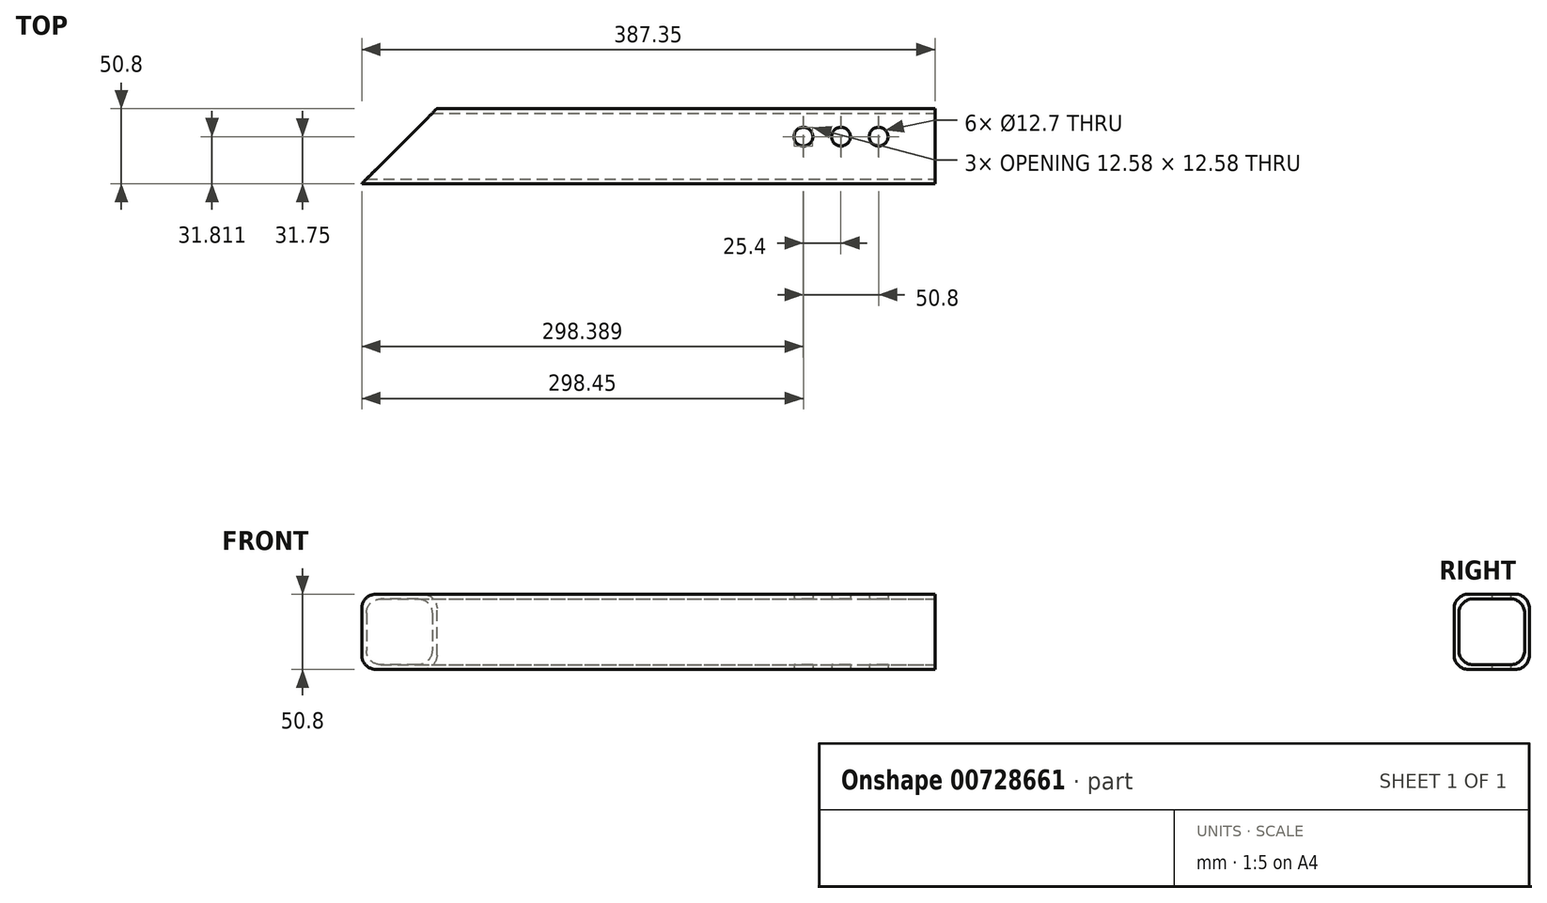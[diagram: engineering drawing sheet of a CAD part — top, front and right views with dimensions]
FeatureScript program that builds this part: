
annotation { "Feature Type Name" : "Feature", "Feature Type Description" : "" }
export const myFeature = defineFeature(function(context is Context, id is Id, definition is map)
    precondition{}
    {
        {
            var Q0;
            Q0=qCreatedBy(makeId("Right.planeOp"),FACE);
            var sketch = newSketch(context, id + "F0", { "sketchPlane" : qUnion([Q0])});
            skLineSegment(sketch, "E0.bottom", {"start": v(0, 0) * mm, "end": v(50.8, 0) * mm});
            skLineSegment(sketch, "E0.top", {"start": v(0, 50.8) * mm, "end": v(50.8, 50.8) * mm});
            skLineSegment(sketch, "E0.left", {"start": v(0, 0) * mm, "end": v(0, 50.8) * mm});
            skLineSegment(sketch, "E0.right", {"start": v(50.8, 0) * mm, "end": v(50.8, 50.8) * mm});
            skSolve(sketch);
        }
        {
            var Q0;
            Q0=qSketchRegion(id+"F0",true);
            extrude(context, id + "F1", {"entities" : qUnion([Q0]), "oppositeDirection" : true, "depth" : 387.35 * mm, "offsetDistance" : 25.4 * mm});
        }
        {
            var Q0;
            Q0=makeQuery(id+"F1.opExtrude","CAP_EDGE",EDGE,{"disambiguationData":[OSD([sQuery(id+"F0.wireOp",EDGE,"E0.right")])],"isStart":false});
            chamfer(context, id + "F2", {"entities" : qUnion([Q0]), "width" : 50.8 * mm, "tangentPropagation" : true});
        }
        {
            var Q0;
            Q0=makeQuery(id+"F1.opExtrude","CAP_FACE",FACE,{"disambiguationData":[OSD([sQuery(id+"F0.wireOp",EDGE,"E0.bottom"),sQuery(id+"F0.wireOp",EDGE,"E0.top"),sQuery(id+"F0.wireOp",EDGE,"E0.left"),sQuery(id+"F0.wireOp",EDGE,"E0.right")])],"isStart":true});
            var sketch = newSketch(context, id + "F3", { "sketchPlane" : qUnion([Q0])});
            skLineSegment(sketch, "E1.0", {"start": v(3.17, 47.63) * mm, "end": v(47.63, 47.63) * mm});
            skLineSegment(sketch, "E1.1", {"start": v(3.17, 3.17) * mm, "end": v(3.17, 47.63) * mm});
            skLineSegment(sketch, "E1.2", {"start": v(3.17, 3.17) * mm, "end": v(47.63, 3.17) * mm});
            skLineSegment(sketch, "E1.3", {"start": v(47.63, 3.17) * mm, "end": v(47.63, 47.63) * mm});
            skSolve(sketch);
        }
        {
            var Q0;
            Q0=qSketchRegion(id+"F3",true);
            extrude(context, id + "F4", {"entities" : qUnion([Q0]), "operationType" : NewBodyOperationType.REMOVE, "oppositeDirection" : true, "depth" : 876.3 * mm, "offsetDistance" : 25.4 * mm});
        }
        {
            var Q0;
            Q0=makeQuery(id+"F4.boolean.opBoolean","COPY",EDGE,{"derivedFrom":makeQuery(id+"F4.opExtrude","SWEPT_EDGE",EDGE,{"disambiguationData":[OSD([sQuery(id+"F3.wireOp",EDGE,"E1.1"),sQuery(id+"F3.wireOp",EDGE,"E1.2")])]})});
            var Q1;
            Q1=makeQuery(id+"F4.boolean.opBoolean","COPY",EDGE,{"derivedFrom":makeQuery(id+"F4.opExtrude","SWEPT_EDGE",EDGE,{"disambiguationData":[OSD([sQuery(id+"F3.wireOp",EDGE,"E1.2"),sQuery(id+"F3.wireOp",EDGE,"E1.3")])]})});
            var Q2;
            Q2=makeQuery(id+"F4.boolean.opBoolean","COPY",EDGE,{"derivedFrom":makeQuery(id+"F4.opExtrude","SWEPT_EDGE",EDGE,{"disambiguationData":[OSD([sQuery(id+"F3.wireOp",EDGE,"E1.0"),sQuery(id+"F3.wireOp",EDGE,"E1.3")])]})});
            var Q3;
            Q3=makeQuery(id+"F4.boolean.opBoolean","COPY",EDGE,{"derivedFrom":makeQuery(id+"F4.opExtrude","SWEPT_EDGE",EDGE,{"disambiguationData":[OSD([sQuery(id+"F3.wireOp",EDGE,"E1.0"),sQuery(id+"F3.wireOp",EDGE,"E1.1")])]})});
            var Q4;
            Q4=makeQuery(id+"F1.opExtrude","SWEPT_EDGE",EDGE,{"disambiguationData":[OSD([sQuery(id+"F0.wireOp",EDGE,"E0.bottom"),sQuery(id+"F0.wireOp",EDGE,"E0.right")])]});
            var Q5;
            Q5=makeQuery(id+"F1.opExtrude","SWEPT_EDGE",EDGE,{"disambiguationData":[OSD([sQuery(id+"F0.wireOp",EDGE,"E0.top"),sQuery(id+"F0.wireOp",EDGE,"E0.right")])]});
            var Q6;
            Q6=makeQuery(id+"F1.opExtrude","SWEPT_EDGE",EDGE,{"disambiguationData":[OSD([sQuery(id+"F0.wireOp",EDGE,"E0.top"),sQuery(id+"F0.wireOp",EDGE,"E0.left")])]});
            var Q7;
            Q7=makeQuery(id+"F1.opExtrude","SWEPT_EDGE",EDGE,{"disambiguationData":[OSD([sQuery(id+"F0.wireOp",EDGE,"E0.bottom"),sQuery(id+"F0.wireOp",EDGE,"E0.left")])]});
            fillet(context, id + "F5", {"entities" : qUnion([Q0, Q1, Q2, Q3, Q4, Q5, Q6, Q7]), "radius" : 9.52 * mm, "tangentPropagation" : true, "allowEdgeOverflow" : false});
        }
        {
            var Q0;
            Q0=makeQuery(id+"F1.opExtrude","SWEPT_FACE",FACE,{"disambiguationData":[OSD([sQuery(id+"F0.wireOp",EDGE,"E0.bottom")])]});
            var sketch = newSketch(context, id + "F6", { "sketchPlane" : qUnion([Q0])});
            skLineSegment(sketch, "E2", {"start": v(-38.1, -31.75) * mm, "end": v(-63.5, -31.75) * mm});
            skLineSegment(sketch, "E3", {"start": v(-63.5, -31.75) * mm, "end": v(-88.9, -31.75) * mm});
            skSolve(sketch);
        }
        {
            var Q0;
            Q0=sQuery(id+"F6.wireOp",VERTEX,"E2.start");
            var Q1;
            Q1=sQuery(id+"F6.wireOp",VERTEX,"E2.end");
            var Q2;
            Q2=sQuery(id+"F6.wireOp",VERTEX,"E3.end");
            var Q3;
            Q3=makeQuery(id+"F1.opExtrude","SWEPT_BODY",BODY,{"disambiguationData":[OSD([sQuery(id+"F0.wireOp",EDGE,"E0.bottom"),sQuery(id+"F0.wireOp",EDGE,"E0.top"),sQuery(id+"F0.wireOp",EDGE,"E0.left"),sQuery(id+"F0.wireOp",EDGE,"E0.right")])]});
            hole(context, id + "F7", {"style" : HoleStyle.SIMPLE, "endStyle" : HoleEndStyle.BLIND, "holeDiameter" : 12.7 * mm, "majorDiameter" : 6.35 * mm, "holeDepth" : 127 * mm, "isTappedThrough" : true, "tappedDepth" : 12.7 * mm, "tapClearance" : 3, "locations" : qUnion([Q0, Q1, Q2]), "scope" : qUnion([Q3])});
        }
    });
